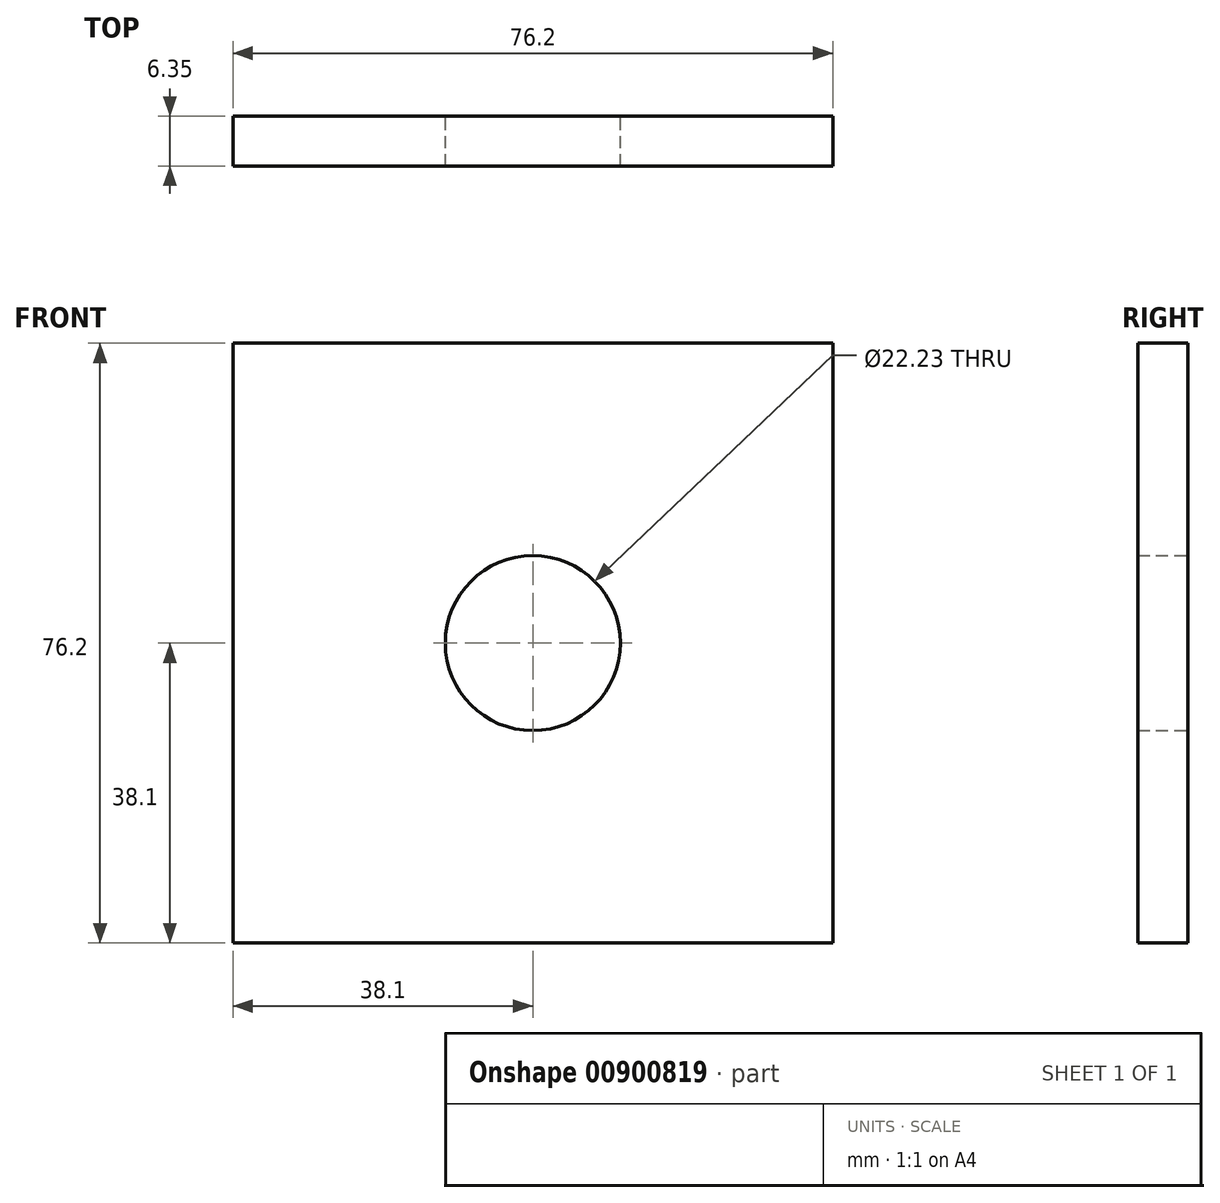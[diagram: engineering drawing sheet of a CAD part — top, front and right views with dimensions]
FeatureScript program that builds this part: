
annotation { "Feature Type Name" : "Feature", "Feature Type Description" : "" }
export const myFeature = defineFeature(function(context is Context, id is Id, definition is map)
    precondition{}
    {
        {
            var Q0;
            Q0=qCreatedBy(makeId("Front.planeOp"),FACE);
            var sketch = newSketch(context, id + "F0", { "sketchPlane" : qUnion([Q0])});
            skLineSegment(sketch, "E0.bottom", {"start": v(38.1, -38.1) * mm, "end": v(-38.1, -38.1) * mm});
            skLineSegment(sketch, "E0.top", {"start": v(38.1, 38.1) * mm, "end": v(-38.1, 38.1) * mm});
            skLineSegment(sketch, "E0.left", {"start": v(38.1, -38.1) * mm, "end": v(38.1, 38.1) * mm});
            skLineSegment(sketch, "E0.right", {"start": v(-38.1, -38.1) * mm, "end": v(-38.1, 38.1) * mm});
            skPoint(sketch, "E0.middle", {"position": v(0, 0) * mm});
            skCircle(sketch, "E1", {"center": v(0, 0) * mm, "radius": 11.11 * mm});
            skSolve(sketch);
        }
        {
            var Q0;
            Q0 = qSketchRegion(id + "F0", true);
            extrude(context, id + "F1", {"entities" : qUnion([Q0]), "depth" : 6.35 * mm, "offsetDistance" : 25.4 * mm});
        }
    });
